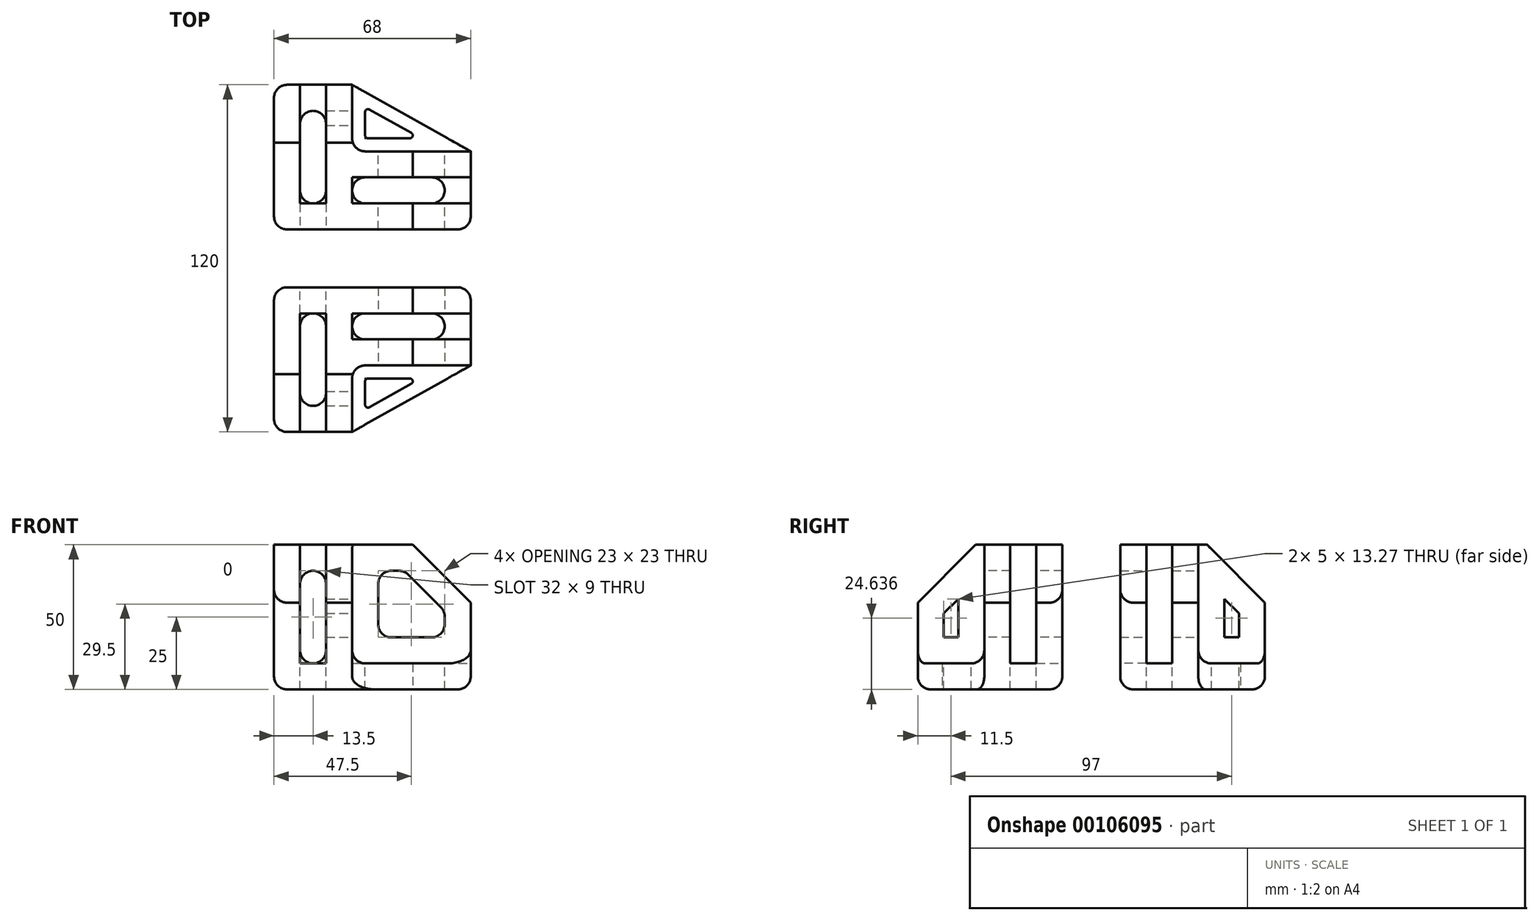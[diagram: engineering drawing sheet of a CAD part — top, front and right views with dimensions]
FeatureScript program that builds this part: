
annotation { "Feature Type Name" : "Feature", "Feature Type Description" : "" }
export const myFeature = defineFeature(function(context is Context, id is Id, definition is map)
    precondition{}
    {
        {
            var Q0;
            Q0=qCreatedBy(makeId("Top.planeOp"),FACE);
            var sketch = newSketch(context, id + "F0", { "sketchPlane" : qUnion([Q0])});
            skLineSegment(sketch, "E0", {"start": v(0, 0) * mm, "end": v(0, 50) * mm});
            skLineSegment(sketch, "E1", {"start": v(0, 50) * mm, "end": v(9, 50) * mm});
            skLineSegment(sketch, "E2", {"start": v(9, 50) * mm, "end": v(9, 9) * mm});
            skLineSegment(sketch, "E3", {"start": v(9, 9) * mm, "end": v(18, 9) * mm});
            skLineSegment(sketch, "E4", {"start": v(18, 9) * mm, "end": v(18, 50) * mm});
            skLineSegment(sketch, "E5", {"start": v(18, 50) * mm, "end": v(27, 50) * mm});
            skLineSegment(sketch, "E6", {"start": v(27, 50) * mm, "end": v(27, 27) * mm});
            skLineSegment(sketch, "E7", {"start": v(27, 27) * mm, "end": v(68, 27) * mm});
            skLineSegment(sketch, "E8", {"start": v(68, 27) * mm, "end": v(68, 18) * mm});
            skLineSegment(sketch, "E9", {"start": v(68, 18) * mm, "end": v(27, 18) * mm});
            skLineSegment(sketch, "E10", {"start": v(27, 18) * mm, "end": v(27, 9) * mm});
            skLineSegment(sketch, "E11", {"start": v(27, 9) * mm, "end": v(68, 9) * mm});
            skLineSegment(sketch, "E12", {"start": v(68, 9) * mm, "end": v(68, 0) * mm});
            skLineSegment(sketch, "E13", {"start": v(68, 0) * mm, "end": v(0, 0) * mm});
            skSolve(sketch);
        }
        {
            var Q0;
            Q0 = qSketchRegion(id + "F0", true);
            extrude(context, id + "F1", {"entities" : qUnion([Q0]), "depth" : 41 * mm});
        }
        {
            var Q0;
            Q0=qCreatedBy(makeId("Top.planeOp"),FACE);
            var sketch = newSketch(context, id + "F2", { "sketchPlane" : qUnion([Q0])});
            skLineSegment(sketch, "E14", {"start": v(0, 0) * mm, "end": v(0, 50) * mm});
            skLineSegment(sketch, "E15", {"start": v(0, 50) * mm, "end": v(27, 50) * mm});
            skLineSegment(sketch, "E16", {"start": v(27, 50) * mm, "end": v(68, 27) * mm});
            skLineSegment(sketch, "E17", {"start": v(68, 27) * mm, "end": v(68, 0) * mm});
            skLineSegment(sketch, "E18", {"start": v(68, 0) * mm, "end": v(0, 0) * mm});
            skSolve(sketch);
        }
        {
            var Q0;
            Q0 = qSketchRegion(id + "F2", true);
            extrude(context, id + "F3", {"entities" : qUnion([Q0]), "operationType" : NewBodyOperationType.ADD, "oppositeDirection" : true, "depth" : 9 * mm});
        }
        {
            var Q0;
            {var subQ0=sQuery(id+"F2.wireOp",EDGE,"E15");var subQ1=sQuery(id+"F2.wireOp",EDGE,"E16");var subQ2=sQuery(id+"F2.wireOp",EDGE,"E17");Q0=makeQuery(id+"F3.boolean.opBoolean","SPLIT",FACE,{"disambiguationData":[TD([makeQuery(id+"F1.opExtrude","SWEPT_FACE",FACE,{"disambiguationData":[OSD([sQuery(id+"F0.wireOp",EDGE,"E6")])]})])],"derivedFrom":makeQuery(id+"F3.opExtrude","CAP_FACE",FACE,{"disambiguationData":[OSD([sQuery(id+"F2.wireOp",EDGE,"E14"),subQ0,subQ1,subQ2,sQuery(id+"F2.wireOp",EDGE,"E18")])],"isStart":true})});}
            var sketch = newSketch(context, id + "F4", { "sketchPlane" : qUnion([Q0])});
            skLineSegment(sketch, "E19", {"start": v(31.5, 42.32) * mm, "end": v(50.78, 31.5) * mm});
            skLineSegment(sketch, "E20", {"start": v(50.78, 31.5) * mm, "end": v(31.5, 31.5) * mm});
            skLineSegment(sketch, "E21", {"start": v(31.5, 31.5) * mm, "end": v(31.5, 42.32) * mm});
            skSolve(sketch);
        }
        {
            var Q0;
            Q0 = qSketchRegion(id + "F4", true);
            extrude(context, id + "F5", {"entities" : qUnion([Q0]), "operationType" : NewBodyOperationType.REMOVE, "endBound" : BoundingType.UP_TO_NEXT, "oppositeDirection" : true, "depth" : 25 * mm});
        }
        {
            var Q0;
            Q0=makeQuery(id+"F3.boolean.opBoolean","MERGE",FACE,{"derivedFrom":[makeQuery(id+"F1.opExtrude","SWEPT_FACE",FACE,{"disambiguationData":[OSD([sQuery(id+"F0.wireOp",EDGE,"E0")])]}),makeQuery(id+"F3.opExtrude","SWEPT_FACE",FACE,{"disambiguationData":[OSD([sQuery(id+"F2.wireOp",EDGE,"E14")])]})]});
            var sketch = newSketch(context, id + "F6", { "sketchPlane" : qUnion([Q0])});
            skLineSegment(sketch, "E22", {"start": v(-30, 41) * mm, "end": v(-50, 21) * mm});
            skLineSegment(sketch, "E23", {"start": v(-50, 21) * mm, "end": v(-50, 41) * mm});
            skLineSegment(sketch, "E24", {"start": v(-50, 41) * mm, "end": v(-30, 41) * mm});
            skSolve(sketch);
        }
        {
            var Q0;
            Q0 = qSketchRegion(id + "F6", true);
            extrude(context, id + "F7", {"entities" : qUnion([Q0]), "operationType" : NewBodyOperationType.REMOVE, "oppositeDirection" : true, "depth" : 30 * mm});
        }
        {
            var Q0;
            Q0=makeQuery(id+"F3.boolean.opBoolean","MERGE",FACE,{"derivedFrom":[makeQuery(id+"F1.opExtrude","SWEPT_FACE",FACE,{"disambiguationData":[OSD([sQuery(id+"F0.wireOp",EDGE,"E13")])]}),makeQuery(id+"F3.opExtrude","SWEPT_FACE",FACE,{"disambiguationData":[OSD([sQuery(id+"F2.wireOp",EDGE,"E18")])]})]});
            var sketch = newSketch(context, id + "F8", { "sketchPlane" : qUnion([Q0])});
            skLineSegment(sketch, "E25", {"start": v(68, 41) * mm, "end": v(48, 41) * mm});
            skLineSegment(sketch, "E26", {"start": v(48, 41) * mm, "end": v(68, 21) * mm});
            skLineSegment(sketch, "E27", {"start": v(68, 21) * mm, "end": v(68, 41) * mm});
            skSolve(sketch);
        }
        {
            var Q0;
            Q0 = qSketchRegion(id + "F8", true);
            extrude(context, id + "F9", {"entities" : qUnion([Q0]), "operationType" : NewBodyOperationType.REMOVE, "oppositeDirection" : true, "depth" : 30 * mm});
        }
        {
            var Q0;
            {var subQ0=sQuery(id+"F2.wireOp",EDGE,"E17");Q0=makeQuery(id+"F3.boolean.opBoolean","SPLIT",FACE,{"disambiguationData":[TD([makeQuery(id+"F1.opExtrude","SWEPT_FACE",FACE,{"disambiguationData":[OSD([sQuery(id+"F0.wireOp",EDGE,"E9")])]})])],"derivedFrom":makeQuery(id+"F3.opExtrude","CAP_FACE",FACE,{"disambiguationData":[OSD([sQuery(id+"F2.wireOp",EDGE,"E14"),sQuery(id+"F2.wireOp",EDGE,"E15"),sQuery(id+"F2.wireOp",EDGE,"E16"),subQ0,sQuery(id+"F2.wireOp",EDGE,"E18")])],"isStart":true})});}
            var sketch = newSketch(context, id + "F10", { "sketchPlane" : qUnion([Q0])});
            skLineSegment(sketch, "E28", {"start": v(31.5, 18) * mm, "end": v(54.5, 18) * mm});
            skLineSegment(sketch, "E29", {"start": v(59, 13.5) * mm, "end": v(59, 13.5) * mm});
            skLineSegment(sketch, "E30", {"start": v(54.5, 9) * mm, "end": v(31.5, 9) * mm});
            skLineSegment(sketch, "E31", {"start": v(27, 13.5) * mm, "end": v(27, 13.5) * mm});
            skLineSegment(sketch, "E32.bottom", {"start": v(13.5, 9) * mm, "end": v(13.5, 9) * mm});
            skLineSegment(sketch, "E32.top", {"start": v(13.5, 41) * mm, "end": v(13.5, 41) * mm});
            skLineSegment(sketch, "E32.left", {"start": v(9, 13.5) * mm, "end": v(9, 36.5) * mm});
            skLineSegment(sketch, "E32.right", {"start": v(18, 13.5) * mm, "end": v(18, 36.5) * mm});
            skPoint(sketch, "E33.visualSharp", {"position": v(9, 41) * mm});
            skArc(sketch, "E33.filletArc", {"start": v(13.5, 41) * mm, "mid": v(10.32, 39.68) * mm, "end": v(9, 36.5) * mm});
            skPoint(sketch, "E34.visualSharp", {"position": v(18, 41) * mm});
            skArc(sketch, "E34.filletArc", {"start": v(18, 36.5) * mm, "mid": v(16.68, 39.68) * mm, "end": v(13.5, 41) * mm});
            skPoint(sketch, "E35.visualSharp", {"position": v(18, 9) * mm});
            skArc(sketch, "E35.filletArc", {"start": v(13.5, 9) * mm, "mid": v(16.68, 10.32) * mm, "end": v(18, 13.5) * mm});
            skPoint(sketch, "E36.visualSharp", {"position": v(9, 9) * mm});
            skArc(sketch, "E36.filletArc", {"start": v(9, 13.5) * mm, "mid": v(10.32, 10.32) * mm, "end": v(13.5, 9) * mm});
            skPoint(sketch, "E37.visualSharp", {"position": v(59, 18) * mm});
            skArc(sketch, "E37.filletArc", {"start": v(59, 13.5) * mm, "mid": v(57.68, 16.68) * mm, "end": v(54.5, 18) * mm});
            skPoint(sketch, "E38.visualSharp", {"position": v(59, 9) * mm});
            skArc(sketch, "E38.filletArc", {"start": v(54.5, 9) * mm, "mid": v(57.68, 10.32) * mm, "end": v(59, 13.5) * mm});
            skPoint(sketch, "E39.visualSharp", {"position": v(27, 18) * mm});
            skArc(sketch, "E39.filletArc", {"start": v(31.5, 18) * mm, "mid": v(28.32, 16.68) * mm, "end": v(27, 13.5) * mm});
            skPoint(sketch, "E40.visualSharp", {"position": v(27, 9) * mm});
            skArc(sketch, "E40.filletArc", {"start": v(27, 13.5) * mm, "mid": v(28.32, 10.32) * mm, "end": v(31.5, 9) * mm});
            skSolve(sketch);
        }
        {
            var Q0;
            Q0 = qSketchRegion(id + "F10", true);
            extrude(context, id + "F11", {"entities" : qUnion([Q0]), "operationType" : NewBodyOperationType.REMOVE, "endBound" : BoundingType.UP_TO_NEXT, "oppositeDirection" : true, "depth" : 25 * mm});
        }
        {
            var Q0;
            Q0=makeQuery(id+"F1.opExtrude","SWEPT_EDGE",EDGE,{"disambiguationData":[OSD([sQuery(id+"F0.wireOp",EDGE,"E6"),sQuery(id+"F0.wireOp",EDGE,"E7")])]});
            var Q1;
            Q1=makeQuery(id+"F3.boolean.opBoolean","MERGE",EDGE,{"derivedFrom":[makeQuery(id+"F1.opExtrude","SWEPT_EDGE",EDGE,{"disambiguationData":[OSD([sQuery(id+"F0.wireOp",EDGE,"E0"),sQuery(id+"F0.wireOp",EDGE,"E13")])]}),makeQuery(id+"F3.opExtrude","SWEPT_EDGE",EDGE,{"disambiguationData":[OSD([sQuery(id+"F2.wireOp",EDGE,"E14"),sQuery(id+"F2.wireOp",EDGE,"E18")])]})]});
            fillet(context, id + "F12", {"entities" : qUnion([Q0, Q1]), "radius" : 4.5 * mm, "tangentPropagation" : true, "allowEdgeOverflow" : false});
        }
        {
            var Q0;
            Q0=makeQuery(id+"F3.boolean.opBoolean","MERGE",FACE,{"derivedFrom":[makeQuery(id+"F1.opExtrude","SWEPT_FACE",FACE,{"disambiguationData":[OSD([sQuery(id+"F0.wireOp",EDGE,"E13")])]}),makeQuery(id+"F3.opExtrude","SWEPT_FACE",FACE,{"disambiguationData":[OSD([sQuery(id+"F2.wireOp",EDGE,"E18")])]})]});
            var sketch = newSketch(context, id + "F13", { "sketchPlane" : qUnion([Q0])});
            skLineSegment(sketch, "E41", {"start": v(9, 27.5) * mm, "end": v(9, 4.5) * mm});
            skLineSegment(sketch, "E42", {"start": v(13.5, 0) * mm, "end": v(13.5, 0) * mm});
            skLineSegment(sketch, "E43", {"start": v(18, 4.5) * mm, "end": v(18, 27.5) * mm});
            skLineSegment(sketch, "E44", {"start": v(13.5, 32) * mm, "end": v(13.5, 32) * mm});
            skPoint(sketch, "E45.visualSharp", {"position": v(9, 32) * mm});
            skArc(sketch, "E45.filletArc", {"start": v(13.5, 32) * mm, "mid": v(10.32, 30.68) * mm, "end": v(9, 27.5) * mm});
            skPoint(sketch, "E46.visualSharp", {"position": v(18, 32) * mm});
            skArc(sketch, "E46.filletArc", {"start": v(18, 27.5) * mm, "mid": v(16.68, 30.68) * mm, "end": v(13.5, 32) * mm});
            skPoint(sketch, "E47.visualSharp", {"position": v(18, 0) * mm});
            skArc(sketch, "E47.filletArc", {"start": v(13.5, 0) * mm, "mid": v(16.68, 1.32) * mm, "end": v(18, 4.5) * mm});
            skPoint(sketch, "E48.visualSharp", {"position": v(9, 0) * mm});
            skArc(sketch, "E48.filletArc", {"start": v(9, 4.5) * mm, "mid": v(10.32, 1.32) * mm, "end": v(13.5, 0) * mm});
            skSolve(sketch);
        }
        {
            var Q0;
            Q0=makeQuery(id+"F1.opExtrude","SWEPT_FACE",FACE,{"disambiguationData":[OSD([sQuery(id+"F0.wireOp",EDGE,"E7")])]});
            var sketch = newSketch(context, id + "F14", { "sketchPlane" : qUnion([Q0])});
            skLineSegment(sketch, "E49", {"start": v(-59, 9) * mm, "end": v(-59, 18.07) * mm});
            skLineSegment(sketch, "E50", {"start": v(-59, 18.07) * mm, "end": v(-45.07, 32) * mm});
            skLineSegment(sketch, "E51", {"start": v(-45.07, 32) * mm, "end": v(-36, 32) * mm});
            skLineSegment(sketch, "E52", {"start": v(-36, 32) * mm, "end": v(-36, 9) * mm});
            skLineSegment(sketch, "E53", {"start": v(-36, 9) * mm, "end": v(-59, 9) * mm});
            skSolve(sketch);
        }
        {
            var Q0;
            Q0 = qSketchRegion(id + "F14", true);
            extrude(context, id + "F15", {"entities" : qUnion([Q0]), "operationType" : NewBodyOperationType.REMOVE, "oppositeDirection" : true, "depth" : 30 * mm});
        }
        {
            var Q0;
            Q0=makeQuery(id+"F1.opExtrude","SWEPT_FACE",FACE,{"disambiguationData":[OSD([sQuery(id+"F0.wireOp",EDGE,"E6")])]});
            var sketch = newSketch(context, id + "F16", { "sketchPlane" : qUnion([Q0])});
            skLineSegment(sketch, "E54", {"start": v(36, 9) * mm, "end": v(36, 22.27) * mm});
            skLineSegment(sketch, "E55", {"start": v(36, 22.27) * mm, "end": v(41, 17.27) * mm});
            skLineSegment(sketch, "E56", {"start": v(41, 17.27) * mm, "end": v(41, 9) * mm});
            skLineSegment(sketch, "E57", {"start": v(41, 9) * mm, "end": v(36, 9) * mm});
            skSolve(sketch);
        }
        {
            var Q0;
            Q0 = qSketchRegion(id + "F16", true);
            extrude(context, id + "F17", {"entities" : qUnion([Q0]), "operationType" : NewBodyOperationType.REMOVE, "endBound" : BoundingType.UP_TO_NEXT, "oppositeDirection" : true, "depth" : 30 * mm});
        }
        {
            var Q0;
            Q0=makeQuery(id+"F13.imprint","IMPRINT",FACE,{"disambiguationData":[TD([[makeQuery(id+"F13.imprint","IMPRINT",EDGE,{"derivedFrom":sQuery(id+"F13.wireOp",EDGE,"E41")}),1.0]])]});
            extrude(context, id + "F18", {"entities" : qUnion([Q0]), "operationType" : NewBodyOperationType.REMOVE, "oppositeDirection" : true, "depth" : 25 * mm});
        }
        {
            var Q0;
            Q0=makeQuery(id+"F1.opExtrude","CAP_EDGE",EDGE,{"disambiguationData":[OSD([sQuery(id+"F0.wireOp",EDGE,"E6")])],"isStart":true});
            var Q1;
            {var subQ0=sQuery(id+"F2.wireOp",EDGE,"E15");var subQ1=sQuery(id+"F0.wireOp",EDGE,"E7");var subQ2=sQuery(id+"F2.wireOp",EDGE,"E16");var subQ3=sQuery(id+"F0.wireOp",EDGE,"E6");var subQ4=sQuery(id+"F2.wireOp",EDGE,"E17");Q1=makeQuery(id+"F12.opFillet","BLEND_EDGE",EDGE,{"blendedFrom":[makeQuery(id+"F1.opExtrude","SWEPT_EDGE",EDGE,{"disambiguationData":[OSD([subQ3,subQ1])]}),makeQuery(id+"F3.boolean.opBoolean","SPLIT",FACE,{"disambiguationData":[TD([makeQuery(id+"F1.opExtrude","SWEPT_FACE",FACE,{"disambiguationData":[OSD([subQ3])]})])],"derivedFrom":makeQuery(id+"F3.opExtrude","CAP_FACE",FACE,{"disambiguationData":[OSD([sQuery(id+"F2.wireOp",EDGE,"E14"),subQ0,subQ2,subQ4,sQuery(id+"F2.wireOp",EDGE,"E18")])],"isStart":true})})],"blendedInto":[makeQuery(id+"F3.boolean.opBoolean","SPLIT",FACE,{"disambiguationData":[TD([makeQuery(id+"F1.opExtrude","SWEPT_FACE",FACE,{"disambiguationData":[OSD([subQ3])]})])],"derivedFrom":makeQuery(id+"F3.opExtrude","CAP_FACE",FACE,{"disambiguationData":[OSD([sQuery(id+"F2.wireOp",EDGE,"E14"),subQ0,subQ2,subQ4,sQuery(id+"F2.wireOp",EDGE,"E18")])],"isStart":true})})]});}
            var Q2;
            Q2=makeQuery(id+"F1.opExtrude","CAP_EDGE",EDGE,{"disambiguationData":[OSD([sQuery(id+"F0.wireOp",EDGE,"E7")])],"isStart":true});
            fillet(context, id + "F19", {"entities" : qUnion([Q0, Q1, Q2]), "radius" : 4.5 * mm, "tangentPropagation" : true, "allowEdgeOverflow" : false});
        }
        {
            var Q0;
            Q0=makeQuery(id+"F5.boolean.opBoolean","COPY",EDGE,{"derivedFrom":makeQuery(id+"F5.opExtrude","SWEPT_EDGE",EDGE,{"disambiguationData":[OSD([sQuery(id+"F4.wireOp",EDGE,"E20"),sQuery(id+"F4.wireOp",EDGE,"E21")])]})});
            var Q1;
            Q1=makeQuery(id+"F5.boolean.opBoolean","COPY",EDGE,{"derivedFrom":makeQuery(id+"F5.opExtrude","SWEPT_EDGE",EDGE,{"disambiguationData":[OSD([sQuery(id+"F4.wireOp",EDGE,"E19"),sQuery(id+"F4.wireOp",EDGE,"E21")])]})});
            var Q2;
            Q2=makeQuery(id+"F5.boolean.opBoolean","COPY",EDGE,{"derivedFrom":makeQuery(id+"F5.opExtrude","SWEPT_EDGE",EDGE,{"disambiguationData":[OSD([sQuery(id+"F4.wireOp",EDGE,"E19"),sQuery(id+"F4.wireOp",EDGE,"E20")])]})});
            fillet(context, id + "F20", {"entities" : qUnion([Q0, Q1, Q2]), "radius" : 1 * mm, "tangentPropagation" : true, "allowEdgeOverflow" : false});
        }
        {
            var Q0;
            Q0=makeQuery(id+"F3.boolean.opBoolean","MERGE",EDGE,{"derivedFrom":[makeQuery(id+"F1.opExtrude","SWEPT_EDGE",EDGE,{"disambiguationData":[OSD([sQuery(id+"F0.wireOp",EDGE,"E0"),sQuery(id+"F0.wireOp",EDGE,"E1")])]}),makeQuery(id+"F3.opExtrude","SWEPT_EDGE",EDGE,{"disambiguationData":[OSD([sQuery(id+"F2.wireOp",EDGE,"E14"),sQuery(id+"F2.wireOp",EDGE,"E15")])]})]});
            var Q1;
            Q1=makeQuery(id+"F3.boolean.opBoolean","MERGE",EDGE,{"derivedFrom":[makeQuery(id+"F1.opExtrude","SWEPT_EDGE",EDGE,{"disambiguationData":[OSD([sQuery(id+"F0.wireOp",EDGE,"E12"),sQuery(id+"F0.wireOp",EDGE,"E13")])]}),makeQuery(id+"F3.opExtrude","SWEPT_EDGE",EDGE,{"disambiguationData":[OSD([sQuery(id+"F2.wireOp",EDGE,"E17"),sQuery(id+"F2.wireOp",EDGE,"E18")])]})]});
            fillet(context, id + "F21", {"entities" : qUnion([Q0, Q1]), "radius" : 4.5 * mm, "tangentPropagation" : true, "allowEdgeOverflow" : false});
        }
        {
            var Q0;
            Q0=makeQuery(id+"F15.boolean.opBoolean","COPY",EDGE,{"disambiguationData":[OD(0.0)],"derivedFrom":makeQuery(id+"F15.opExtrude","SWEPT_EDGE",EDGE,{"disambiguationData":[OSD([sQuery(id+"F14.wireOp",EDGE,"E52"),sQuery(id+"F14.wireOp",EDGE,"E53")])]})});
            var Q1;
            Q1=makeQuery(id+"F15.boolean.opBoolean","COPY",EDGE,{"disambiguationData":[OD(1.0)],"derivedFrom":makeQuery(id+"F15.opExtrude","SWEPT_EDGE",EDGE,{"disambiguationData":[OSD([sQuery(id+"F14.wireOp",EDGE,"E52"),sQuery(id+"F14.wireOp",EDGE,"E53")])]})});
            var Q2;
            Q2=makeQuery(id+"F15.boolean.opBoolean","COPY",EDGE,{"disambiguationData":[OD(1.0)],"derivedFrom":makeQuery(id+"F15.opExtrude","SWEPT_EDGE",EDGE,{"disambiguationData":[OSD([sQuery(id+"F14.wireOp",EDGE,"E49"),sQuery(id+"F14.wireOp",EDGE,"E53")])]})});
            var Q3;
            Q3=makeQuery(id+"F15.boolean.opBoolean","COPY",EDGE,{"disambiguationData":[OD(0.0)],"derivedFrom":makeQuery(id+"F15.opExtrude","SWEPT_EDGE",EDGE,{"disambiguationData":[OSD([sQuery(id+"F14.wireOp",EDGE,"E49"),sQuery(id+"F14.wireOp",EDGE,"E53")])]})});
            var Q4;
            Q4=makeQuery(id+"F15.boolean.opBoolean","COPY",EDGE,{"disambiguationData":[OD(0.0)],"derivedFrom":makeQuery(id+"F15.opExtrude","SWEPT_EDGE",EDGE,{"disambiguationData":[OSD([sQuery(id+"F14.wireOp",EDGE,"E49"),sQuery(id+"F14.wireOp",EDGE,"E50")])]})});
            var Q5;
            Q5=makeQuery(id+"F15.boolean.opBoolean","COPY",EDGE,{"disambiguationData":[OD(1.0)],"derivedFrom":makeQuery(id+"F15.opExtrude","SWEPT_EDGE",EDGE,{"disambiguationData":[OSD([sQuery(id+"F14.wireOp",EDGE,"E49"),sQuery(id+"F14.wireOp",EDGE,"E50")])]})});
            var Q6;
            Q6=makeQuery(id+"F15.boolean.opBoolean","COPY",EDGE,{"disambiguationData":[OD(0.0)],"derivedFrom":makeQuery(id+"F15.opExtrude","SWEPT_EDGE",EDGE,{"disambiguationData":[OSD([sQuery(id+"F14.wireOp",EDGE,"E50"),sQuery(id+"F14.wireOp",EDGE,"E51")])]})});
            var Q7;
            Q7=makeQuery(id+"F15.boolean.opBoolean","COPY",EDGE,{"disambiguationData":[OD(1.0)],"derivedFrom":makeQuery(id+"F15.opExtrude","SWEPT_EDGE",EDGE,{"disambiguationData":[OSD([sQuery(id+"F14.wireOp",EDGE,"E50"),sQuery(id+"F14.wireOp",EDGE,"E51")])]})});
            var Q8;
            Q8=makeQuery(id+"F15.boolean.opBoolean","COPY",EDGE,{"disambiguationData":[OD(0.0)],"derivedFrom":makeQuery(id+"F15.opExtrude","SWEPT_EDGE",EDGE,{"disambiguationData":[OSD([sQuery(id+"F14.wireOp",EDGE,"E51"),sQuery(id+"F14.wireOp",EDGE,"E52")])]})});
            var Q9;
            Q9=makeQuery(id+"F15.boolean.opBoolean","COPY",EDGE,{"disambiguationData":[OD(1.0)],"derivedFrom":makeQuery(id+"F15.opExtrude","SWEPT_EDGE",EDGE,{"disambiguationData":[OSD([sQuery(id+"F14.wireOp",EDGE,"E51"),sQuery(id+"F14.wireOp",EDGE,"E52")])]})});
            fillet(context, id + "F22", {"entities" : qUnion([Q0, Q1, Q2, Q3, Q4, Q5, Q6, Q7, Q8, Q9]), "radius" : 4.5 * mm, "tangentPropagation" : true, "allowEdgeOverflow" : false});
        }
        {
            var Q0;
            Q0=makeQuery(id+"F3.opExtrude","CAP_EDGE",EDGE,{"disambiguationData":[OSD([sQuery(id+"F2.wireOp",EDGE,"E18")])],"isStart":false});
            fillet(context, id + "F23", {"entities" : qUnion([Q0]), "radius" : 4.5 * mm, "tangentPropagation" : true, "allowEdgeOverflow" : false});
        }
        {
            var Q0;
            Q0=makeQuery(id+"F3.boolean.opBoolean","MERGE",FACE,{"derivedFrom":[makeQuery(id+"F1.opExtrude","SWEPT_FACE",FACE,{"disambiguationData":[OSD([sQuery(id+"F0.wireOp",EDGE,"E13")])]}),makeQuery(id+"F3.opExtrude","SWEPT_FACE",FACE,{"disambiguationData":[OSD([sQuery(id+"F2.wireOp",EDGE,"E18")])]})]});
            cPlane(context, id + "F24", {"entities" : qUnion([Q0]), "cplaneType" : CPlaneType.OFFSET, "offset" : 10 * mm, "width" : 150 * mm, "height" : 150 * mm});
        }
        {
            var Q0;
            Q0=makeQuery(id+"F1.opExtrude","SWEPT_BODY",BODY,{"disambiguationData":[OSD([sQuery(id+"F0.wireOp",EDGE,"E0"),sQuery(id+"F0.wireOp",EDGE,"E1"),sQuery(id+"F0.wireOp",EDGE,"E2"),sQuery(id+"F0.wireOp",EDGE,"E3"),sQuery(id+"F0.wireOp",EDGE,"E4"),sQuery(id+"F0.wireOp",EDGE,"E5"),sQuery(id+"F0.wireOp",EDGE,"E6"),sQuery(id+"F0.wireOp",EDGE,"E7"),sQuery(id+"F0.wireOp",EDGE,"E8"),sQuery(id+"F0.wireOp",EDGE,"E9"),sQuery(id+"F0.wireOp",EDGE,"E10"),sQuery(id+"F0.wireOp",EDGE,"E11"),sQuery(id+"F0.wireOp",EDGE,"E12"),sQuery(id+"F0.wireOp",EDGE,"E13")])]});
            var Q1;
            Q1=qCreatedBy(id+"F24.planeOp",FACE);
            mirror(context, id + "F25", {"entities" : qUnion([Q0]), "mirrorPlane" : qUnion([Q1])});
        }
    });
